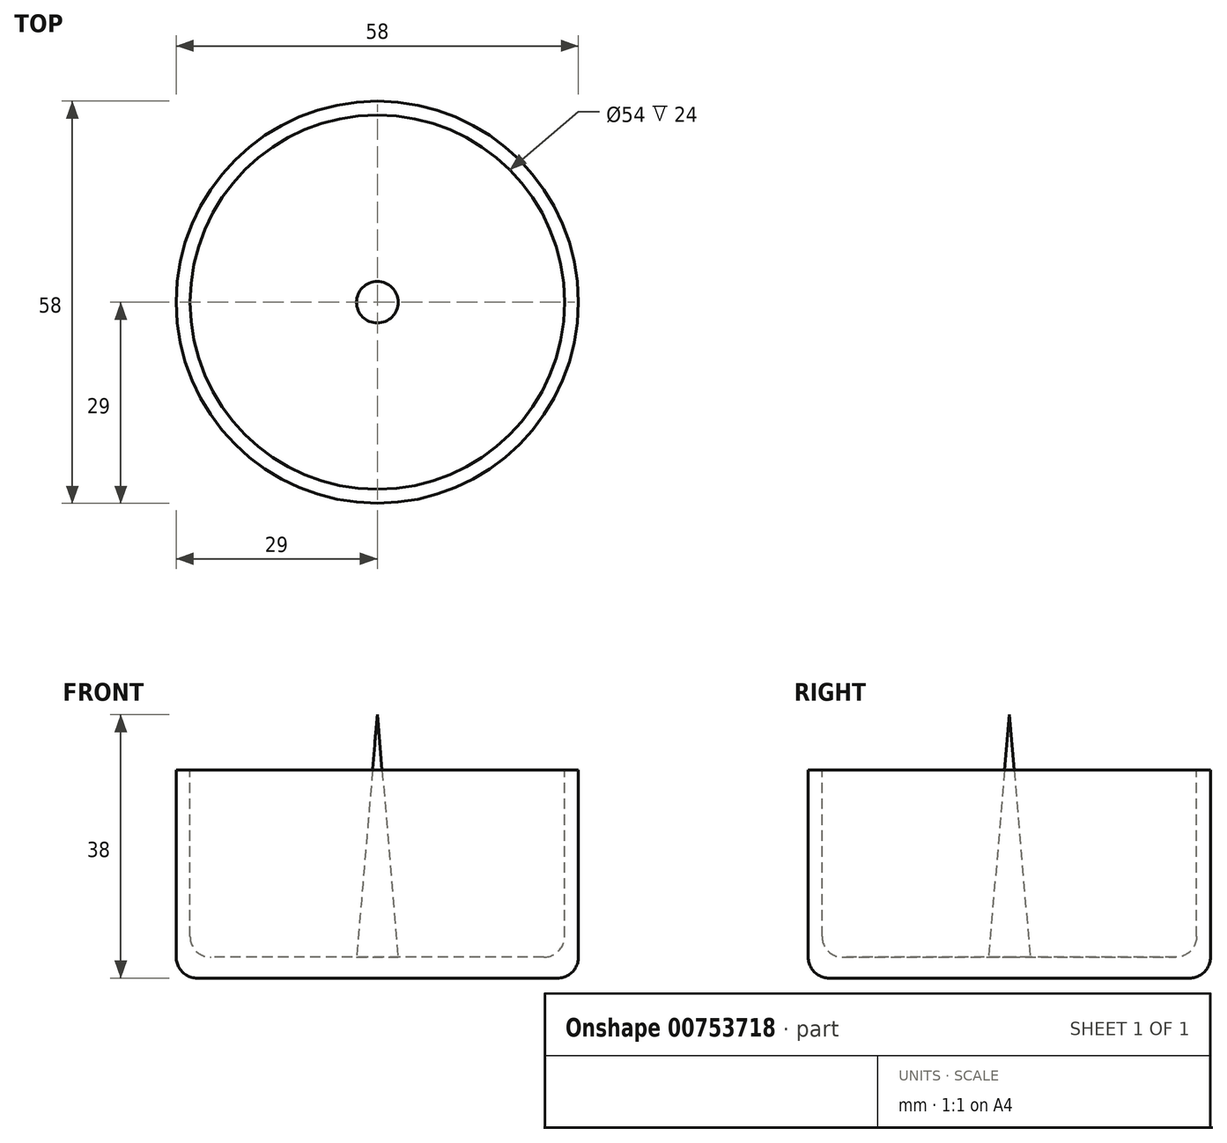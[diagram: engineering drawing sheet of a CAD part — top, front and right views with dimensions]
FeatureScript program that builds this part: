
annotation { "Feature Type Name" : "Feature", "Feature Type Description" : "" }
export const myFeature = defineFeature(function(context is Context, id is Id, definition is map)
    precondition{}
    {
        {
            var Q0;
            Q0=qCreatedBy(makeId("Top.planeOp"),FACE);
            var sketch = newSketch(context, id + "F0", { "sketchPlane" : qUnion([Q0])});
            skCircle(sketch, "E0", {"center": v(0, 0) * mm, "radius": 29 * mm});
            skSolve(sketch);
        }
        {
            var Q0;
            Q0 = qSketchRegion(id + "F0", true);
            extrude(context, id + "F1", {"entities" : qUnion([Q0]), "depth" : 30 * mm, "offsetDistance" : 25 * mm});
        }
        {
            var Q0;
            Q0=makeQuery(id+"F1.opExtrude","CAP_FACE",FACE,{"disambiguationData":[OSD([sQuery(id+"F0.wireOp",EDGE,"E0")])],"isStart":false});
            cPlane(context, id + "F2", {"entities" : qUnion([Q0]), "cplaneType" : CPlaneType.OFFSET, "offset" : 0 * mm, "width" : 150 * mm, "height" : 150 * mm});
        }
        {
            var Q0;
            Q0=qCreatedBy(id+"F2.planeOp",FACE);
            var sketch = newSketch(context, id + "F3", { "sketchPlane" : qUnion([Q0])});
            skCircle(sketch, "E1", {"center": v(0, 0) * mm, "radius": 27 * mm});
            skSolve(sketch);
        }
        {
            var Q0;
            Q0 = qSketchRegion(id + "F3", true);
            extrude(context, id + "F4", {"entities" : qUnion([Q0]), "operationType" : NewBodyOperationType.REMOVE, "oppositeDirection" : true, "depth" : 27 * mm, "offsetDistance" : 25 * mm});
        }
        {
            var Q0;
            Q0=makeQuery(id+"F4.boolean.opBoolean","COPY",EDGE,{"derivedFrom":makeQuery(id+"F4.opExtrude","CAP_EDGE",EDGE,{"disambiguationData":[OSD([sQuery(id+"F3.wireOp",EDGE,"E1")])],"isStart":false})});
            fillet(context, id + "F5", {"entities" : qUnion([Q0]), "radius" : 3 * mm, "tangentPropagation" : true, "allowEdgeOverflow" : false});
        }
        {
            var Q0;
            Q0=makeQuery(id+"F1.opExtrude","CAP_EDGE",EDGE,{"disambiguationData":[OSD([sQuery(id+"F0.wireOp",EDGE,"E0")])],"isStart":true});
            fillet(context, id + "F6", {"entities" : qUnion([Q0]), "radius" : 3 * mm, "tangentPropagation" : true, "allowEdgeOverflow" : false});
        }
        {
            var Q0;
            Q0=qCreatedBy(makeId("Right.planeOp"),FACE);
            var sketch = newSketch(context, id + "F7", { "sketchPlane" : qUnion([Q0])});
            skLineSegment(sketch, "E2", {"start": v(0, 3) * mm, "end": v(0, 38) * mm});
            skLineSegment(sketch, "E3", {"start": v(0, 38) * mm, "end": v(-3, 3) * mm});
            skLineSegment(sketch, "E4", {"start": v(-3, 3) * mm, "end": v(0, 3) * mm});
            skSolve(sketch);
        }
        {
            var Q0;
            Q0 = qSketchRegion(id + "F7", true);
            var Q1;
            Q1=sQuery(id+"F7.wireOp",EDGE,"E2");
            revolve(context, id + "F8", {"operationType" : NewBodyOperationType.ADD, "surfaceOperationType" : NewSurfaceOperationType.NEW, "entities" : qUnion([Q0]), "axis" : qUnion([Q1]), "revolveType" : RevolveType.FULL});
        }
    });
